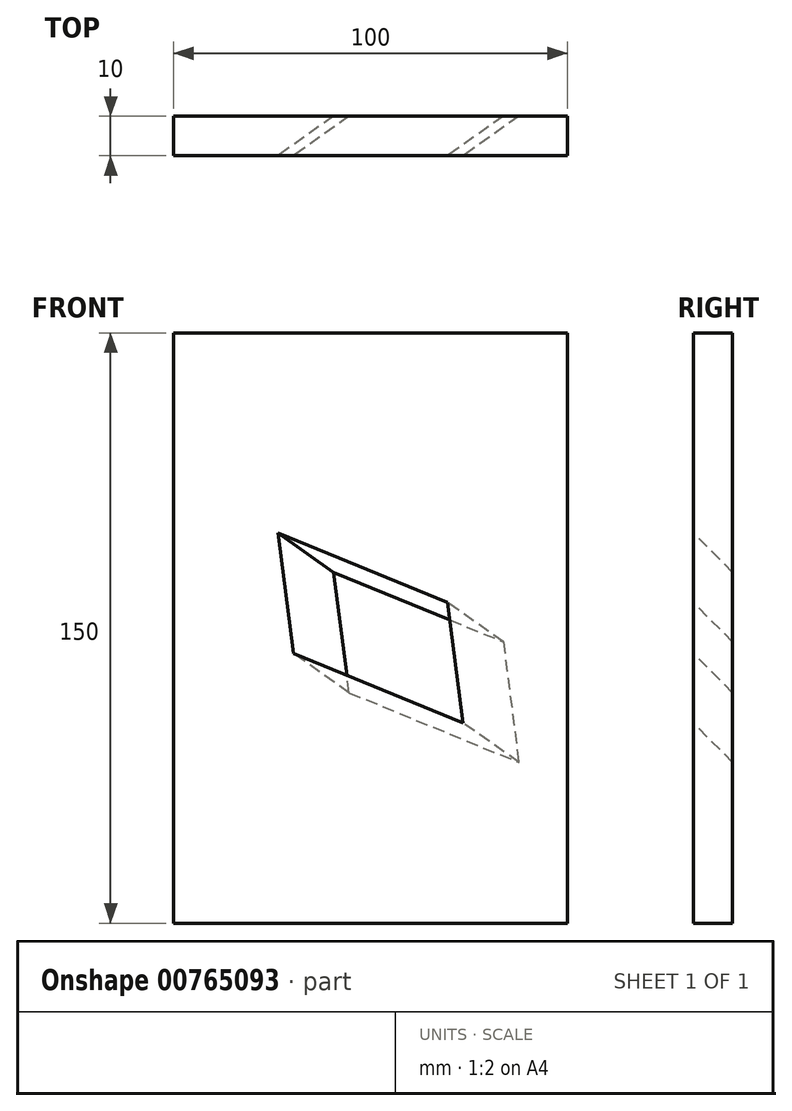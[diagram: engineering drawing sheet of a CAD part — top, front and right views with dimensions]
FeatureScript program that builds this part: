
annotation { "Feature Type Name" : "Feature", "Feature Type Description" : "" }
export const myFeature = defineFeature(function(context is Context, id is Id, definition is map)
    precondition{}
    {
        {
            var Q0;
            Q0=qCreatedBy(makeId("Front.planeOp"),FACE);
            var sketch = newSketch(context, id + "F0", { "sketchPlane" : qUnion([Q0])});
            skLineSegment(sketch, "E0.bottom", {"start": v(50, -75) * mm, "end": v(-50, -75) * mm});
            skLineSegment(sketch, "E0.top", {"start": v(50, 75) * mm, "end": v(-50, 75) * mm});
            skLineSegment(sketch, "E0.left", {"start": v(50, -75) * mm, "end": v(50, 75) * mm});
            skLineSegment(sketch, "E0.right", {"start": v(-50, -75) * mm, "end": v(-50, 75) * mm});
            skPoint(sketch, "E0.middle", {"position": v(0, 0) * mm});
            skSolve(sketch);
        }
        {
            var Q0;
            Q0=qSketchRegion(id+"F0",true);
            extrude(context, id + "F1", {"entities" : qUnion([Q0]), "oppositeDirection" : true, "depth" : 10 * mm, "offsetDistance" : 25 * mm});
        }
        {
            var Q0;
            Q0=qCreatedBy(makeId("Right.planeOp"),FACE);
            var sketch = newSketch(context, id + "F2", { "sketchPlane" : qUnion([Q0])});
            skLineSegment(sketch, "E1", {"start": v(0, 0) * mm, "end": v(-70.71, 70.71) * mm});
            skSolve(sketch);
        }
        {
            var Q0;
            Q0=sQuery(id+"F2.wireOp",EDGE,"E1");
            cPlane(context, id + "F3", {"entities" : qUnion([Q0]), "cplaneType" : CPlaneType.LINE_ANGLE, "offset" : 25 * mm, "angle" : 0 * degree, "width" : 150 * mm, "height" : 150 * mm});
        }
        {
            var Q0;
            Q0=qCreatedBy(id+"F3.planeOp",FACE);
            var sketch = newSketch(context, id + "F4", { "sketchPlane" : qUnion([Q0])});
            skLineSegment(sketch, "E2", {"start": v(0, 0) * mm, "end": v(-35.36, 35.36) * mm});
            skSolve(sketch);
        }
        {
            var Q0;
            Q0=sQuery(id+"F4.wireOp",VERTEX,"E2.end");
            var Q1;
            Q1=sQuery(id+"F4.wireOp",EDGE,"E2");
            cPlane(context, id + "F5", {"entities" : qUnion([Q0, Q1]), "cplaneType" : CPlaneType.LINE_POINT, "offset" : 25 * mm, "width" : 150 * mm, "height" : 150 * mm});
        }
        {
            var Q0;
            Q0=qCreatedBy(id+"F5.planeOp",FACE);
            var sketch = newSketch(context, id + "F6", { "sketchPlane" : qUnion([Q0])});
            skLineSegment(sketch, "E3", {"start": v(0, 0) * mm, "end": v(5.23, -11.35) * mm, "construction": true});
            skLineSegment(sketch, "E4", {"start": v(-6.12, -16.58) * mm, "end": v(16.58, -6.12) * mm});
            skLineSegment(sketch, "E5", {"start": v(-6.12, -16.58) * mm, "end": v(-16.58, 6.12) * mm});
            skLineSegment(sketch, "E6", {"start": v(-16.58, 6.12) * mm, "end": v(6.12, 16.58) * mm});
            skLineSegment(sketch, "E7", {"start": v(6.12, 16.58) * mm, "end": v(16.58, -6.12) * mm});
            skLineSegment(sketch, "E8", {"start": v(-11.35, -5.23) * mm, "end": v(11.35, 5.23) * mm, "construction": true});
            skLineSegment(sketch, "E9", {"start": v(0, 0) * mm, "end": v(66.55, -47.06) * mm, "construction": true});
            skSolve(sketch);
        }
        {
            var Q0;
            Q0=qSketchRegion(id+"F6",true);
            extrude(context, id + "F7", {"entities" : qUnion([Q0]), "operationType" : NewBodyOperationType.REMOVE, "endBound" : BoundingType.THROUGH_ALL, "oppositeDirection" : true, "depth" : 25 * mm, "offsetDistance" : 25 * mm});
        }
    });
